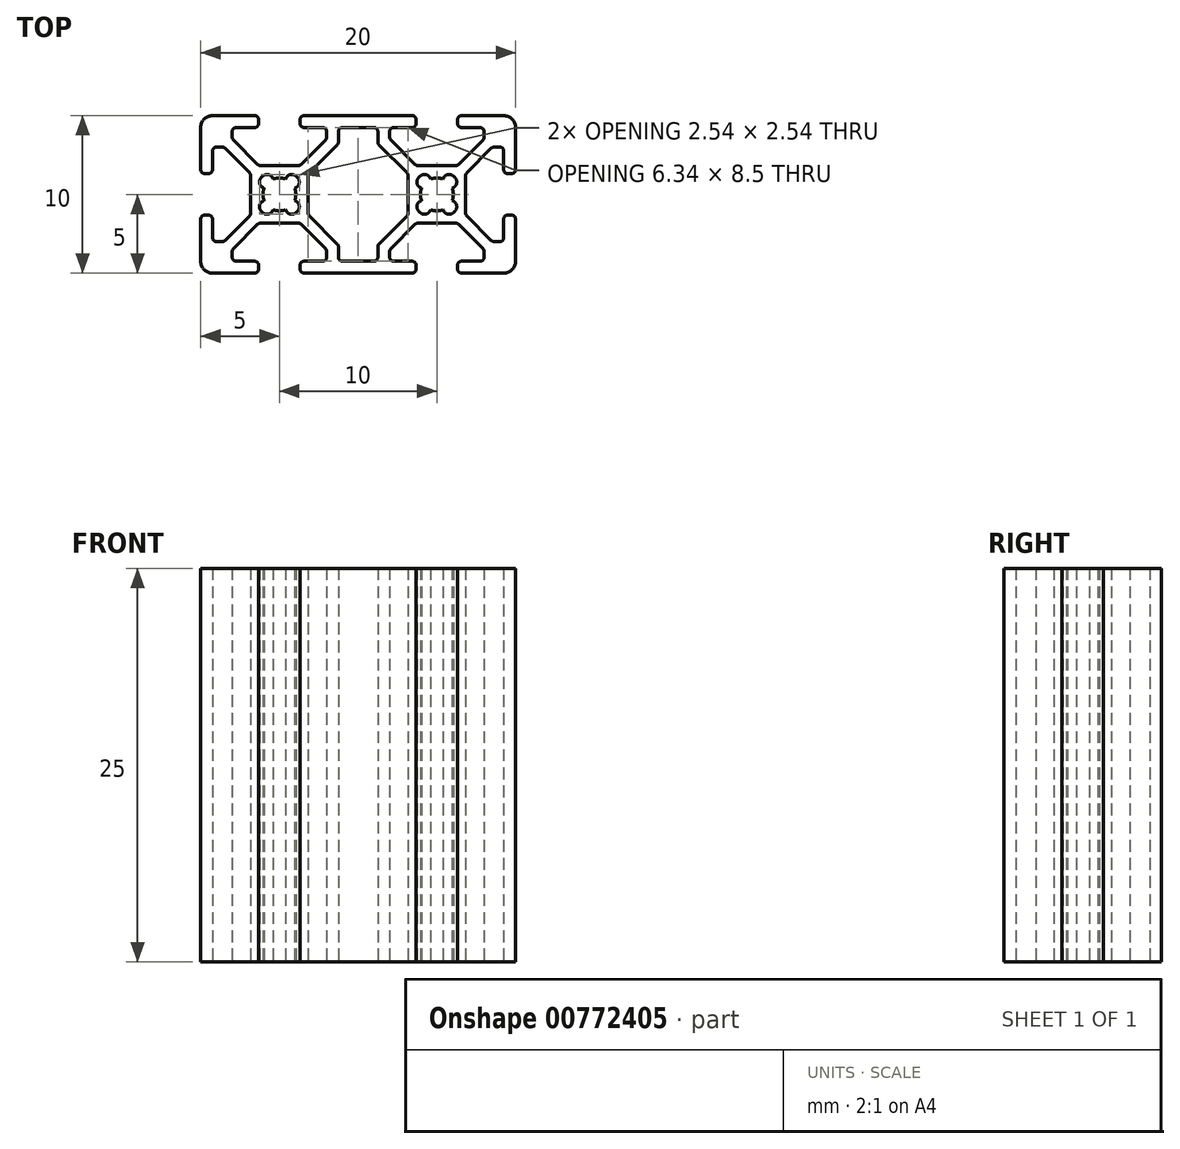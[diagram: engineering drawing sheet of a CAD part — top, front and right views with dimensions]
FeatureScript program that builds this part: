
annotation { "Feature Type Name" : "Feature", "Feature Type Description" : "" }
export const myFeature = defineFeature(function(context is Context, id is Id, definition is map)
    precondition{}
    {
        {
            var Q0;
            Q0=qCreatedBy(makeId("Top.planeOp"),FACE);
            var sketch = newSketch(context, id + "F0", { "sketchPlane" : qUnion([Q0])});
            skArc(sketch, "E0", {"start": v(-6.06, -1.15) * mm, "mid": v(-5.68, -1.25) * mm, "end": v(-5.4, -0.97) * mm});
            skLineSegment(sketch, "E1", {"start": v(-6.15, -1.06) * mm, "end": v(-6.06, -1.15) * mm});
            skArc(sketch, "E2", {"start": v(-5.97, -0.4) * mm, "mid": v(-6.25, -0.68) * mm, "end": v(-6.15, -1.06) * mm});
            skArc(sketch, "E3", {"start": v(-5.97, 0.4) * mm, "mid": v(-6.05, 0) * mm, "end": v(-5.97, -0.4) * mm});
            skArc(sketch, "E4", {"start": v(-6.15, 1.06) * mm, "mid": v(-6.25, 0.68) * mm, "end": v(-5.97, 0.4) * mm});
            skLineSegment(sketch, "E5", {"start": v(-6.06, 1.15) * mm, "end": v(-6.15, 1.06) * mm});
            skArc(sketch, "E6", {"start": v(-5.4, 0.97) * mm, "mid": v(-5.68, 1.25) * mm, "end": v(-6.06, 1.15) * mm});
            skArc(sketch, "E7", {"start": v(-4.6, 0.97) * mm, "mid": v(-5, 1.05) * mm, "end": v(-5.4, 0.97) * mm});
            skArc(sketch, "E8", {"start": v(-3.94, 1.15) * mm, "mid": v(-4.32, 1.25) * mm, "end": v(-4.6, 0.97) * mm});
            skLineSegment(sketch, "E9", {"start": v(-3.85, 1.06) * mm, "end": v(-3.94, 1.15) * mm});
            skArc(sketch, "E10", {"start": v(-4.03, 0.4) * mm, "mid": v(-3.75, 0.68) * mm, "end": v(-3.85, 1.06) * mm});
            skArc(sketch, "E11", {"start": v(-4.03, -0.4) * mm, "mid": v(-3.95, 0) * mm, "end": v(-4.03, 0.4) * mm});
            skArc(sketch, "E12", {"start": v(-3.85, -1.06) * mm, "mid": v(-3.75, -0.68) * mm, "end": v(-4.03, -0.4) * mm});
            skLineSegment(sketch, "E13", {"start": v(-3.94, -1.15) * mm, "end": v(-3.85, -1.06) * mm});
            skArc(sketch, "E14", {"start": v(-4.6, -0.97) * mm, "mid": v(-4.32, -1.25) * mm, "end": v(-3.94, -1.15) * mm});
            skArc(sketch, "E15", {"start": v(-5.4, -0.97) * mm, "mid": v(-5, -1.05) * mm, "end": v(-4.6, -0.97) * mm});
            skArc(sketch, "E16", {"start": v(-1.25, -4) * mm, "mid": v(-1.18, -4.18) * mm, "end": v(-1, -4.25) * mm});
            skLineSegment(sketch, "E17", {"start": v(-1.25, -3.32) * mm, "end": v(-1.25, -4) * mm});
            skArc(sketch, "E18", {"start": v(-1.25, -3.32) * mm, "mid": v(-1.27, -3.23) * mm, "end": v(-1.33, -3.14) * mm});
            skLineSegment(sketch, "E19", {"start": v(-3.1, -1.37) * mm, "end": v(-1.33, -3.14) * mm});
            skArc(sketch, "E20", {"start": v(-3.17, -1.2) * mm, "mid": v(-3.15, -1.29) * mm, "end": v(-3.1, -1.37) * mm});
            skLineSegment(sketch, "E21", {"start": v(-3.17, 1.2) * mm, "end": v(-3.17, -1.2) * mm});
            skArc(sketch, "E22", {"start": v(-3.1, 1.37) * mm, "mid": v(-3.15, 1.29) * mm, "end": v(-3.17, 1.2) * mm});
            skLineSegment(sketch, "E23", {"start": v(-1.33, 3.14) * mm, "end": v(-3.1, 1.37) * mm});
            skArc(sketch, "E24", {"start": v(-1.33, 3.14) * mm, "mid": v(-1.27, 3.23) * mm, "end": v(-1.25, 3.32) * mm});
            skLineSegment(sketch, "E25", {"start": v(-1.25, 4) * mm, "end": v(-1.25, 3.32) * mm});
            skArc(sketch, "E26", {"start": v(-1, 4.25) * mm, "mid": v(-1.18, 4.18) * mm, "end": v(-1.25, 4) * mm});
            skLineSegment(sketch, "E27", {"start": v(1, 4.25) * mm, "end": v(-1, 4.25) * mm});
            skArc(sketch, "E28", {"start": v(1.25, 4) * mm, "mid": v(1.18, 4.18) * mm, "end": v(1, 4.25) * mm});
            skLineSegment(sketch, "E29", {"start": v(1.25, 3.32) * mm, "end": v(1.25, 4) * mm});
            skArc(sketch, "E30", {"start": v(1.25, 3.32) * mm, "mid": v(1.27, 3.23) * mm, "end": v(1.33, 3.14) * mm});
            skLineSegment(sketch, "E31", {"start": v(3.1, 1.37) * mm, "end": v(1.33, 3.14) * mm});
            skArc(sketch, "E32", {"start": v(3.17, 1.2) * mm, "mid": v(3.15, 1.29) * mm, "end": v(3.1, 1.37) * mm});
            skLineSegment(sketch, "E33", {"start": v(3.17, -1.2) * mm, "end": v(3.17, 1.2) * mm});
            skArc(sketch, "E34", {"start": v(3.1, -1.37) * mm, "mid": v(3.15, -1.29) * mm, "end": v(3.17, -1.2) * mm});
            skLineSegment(sketch, "E35", {"start": v(1.33, -3.14) * mm, "end": v(3.1, -1.37) * mm});
            skArc(sketch, "E36", {"start": v(1.33, -3.14) * mm, "mid": v(1.27, -3.23) * mm, "end": v(1.25, -3.32) * mm});
            skLineSegment(sketch, "E37", {"start": v(1.25, -4) * mm, "end": v(1.25, -3.32) * mm});
            skArc(sketch, "E38", {"start": v(1, -4.25) * mm, "mid": v(1.18, -4.18) * mm, "end": v(1.25, -4) * mm});
            skLineSegment(sketch, "E39", {"start": v(-1, -4.25) * mm, "end": v(1, -4.25) * mm});
            skArc(sketch, "E40", {"start": v(3.94, -1.15) * mm, "mid": v(4.32, -1.25) * mm, "end": v(4.6, -0.97) * mm});
            skLineSegment(sketch, "E41", {"start": v(3.85, -1.06) * mm, "end": v(3.94, -1.15) * mm});
            skArc(sketch, "E42", {"start": v(4.03, -0.4) * mm, "mid": v(3.75, -0.68) * mm, "end": v(3.85, -1.06) * mm});
            skArc(sketch, "E43", {"start": v(4.03, 0.4) * mm, "mid": v(3.95, 0) * mm, "end": v(4.03, -0.4) * mm});
            skArc(sketch, "E44", {"start": v(3.85, 1.06) * mm, "mid": v(3.75, 0.68) * mm, "end": v(4.03, 0.4) * mm});
            skLineSegment(sketch, "E45", {"start": v(3.94, 1.15) * mm, "end": v(3.85, 1.06) * mm});
            skArc(sketch, "E46", {"start": v(4.6, 0.97) * mm, "mid": v(4.32, 1.25) * mm, "end": v(3.94, 1.15) * mm});
            skArc(sketch, "E47", {"start": v(5.4, 0.97) * mm, "mid": v(5, 1.05) * mm, "end": v(4.6, 0.97) * mm});
            skArc(sketch, "E48", {"start": v(6.06, 1.15) * mm, "mid": v(5.68, 1.25) * mm, "end": v(5.4, 0.97) * mm});
            skLineSegment(sketch, "E49", {"start": v(6.15, 1.06) * mm, "end": v(6.06, 1.15) * mm});
            skArc(sketch, "E50", {"start": v(5.97, 0.4) * mm, "mid": v(6.25, 0.68) * mm, "end": v(6.15, 1.06) * mm});
            skArc(sketch, "E51", {"start": v(5.97, -0.4) * mm, "mid": v(6.05, 0) * mm, "end": v(5.97, 0.4) * mm});
            skArc(sketch, "E52", {"start": v(6.15, -1.06) * mm, "mid": v(6.25, -0.68) * mm, "end": v(5.97, -0.4) * mm});
            skLineSegment(sketch, "E53", {"start": v(6.06, -1.15) * mm, "end": v(6.15, -1.06) * mm});
            skArc(sketch, "E54", {"start": v(5.4, -0.97) * mm, "mid": v(5.68, -1.25) * mm, "end": v(6.06, -1.15) * mm});
            skArc(sketch, "E55", {"start": v(4.6, -0.97) * mm, "mid": v(5, -1.05) * mm, "end": v(5.4, -0.97) * mm});
            skArc(sketch, "E56", {"start": v(-6.2, -1.83) * mm, "mid": v(-6.29, -1.85) * mm, "end": v(-6.37, -1.9) * mm});
            skLineSegment(sketch, "E57", {"start": v(-6.2, -1.83) * mm, "end": v(-3.8, -1.83) * mm});
            skArc(sketch, "E58", {"start": v(-3.63, -1.9) * mm, "mid": v(-3.71, -1.85) * mm, "end": v(-3.8, -1.83) * mm});
            skLineSegment(sketch, "E59", {"start": v(-3.63, -1.9) * mm, "end": v(-2.08, -3.45) * mm});
            skArc(sketch, "E60", {"start": v(-2, -3.63) * mm, "mid": v(-2.02, -3.54) * mm, "end": v(-2.08, -3.45) * mm});
            skLineSegment(sketch, "E61", {"start": v(-2, -3.63) * mm, "end": v(-2, -4) * mm});
            skArc(sketch, "E62", {"start": v(-2.26, -4.25) * mm, "mid": v(-2.08, -4.18) * mm, "end": v(-2, -4) * mm});
            skLineSegment(sketch, "E63", {"start": v(-2.26, -4.25) * mm, "end": v(-3.43, -4.25) * mm});
            skArc(sketch, "E64", {"start": v(-3.43, -4.25) * mm, "mid": v(-3.61, -4.32) * mm, "end": v(-3.69, -4.5) * mm});
            skLineSegment(sketch, "E65", {"start": v(-3.69, -4.5) * mm, "end": v(-3.69, -4.75) * mm});
            skArc(sketch, "E66", {"start": v(-3.69, -4.75) * mm, "mid": v(-3.61, -4.93) * mm, "end": v(-3.43, -5) * mm});
            skLineSegment(sketch, "E67", {"start": v(-3.43, -5) * mm, "end": v(3.43, -5) * mm});
            skArc(sketch, "E68", {"start": v(3.43, -5) * mm, "mid": v(3.61, -4.93) * mm, "end": v(3.69, -4.75) * mm});
            skLineSegment(sketch, "E69", {"start": v(3.69, -4.75) * mm, "end": v(3.69, -4.5) * mm});
            skArc(sketch, "E70", {"start": v(3.69, -4.5) * mm, "mid": v(3.61, -4.32) * mm, "end": v(3.43, -4.25) * mm});
            skLineSegment(sketch, "E71", {"start": v(3.43, -4.25) * mm, "end": v(2.26, -4.25) * mm});
            skArc(sketch, "E72", {"start": v(2, -4) * mm, "mid": v(2.08, -4.18) * mm, "end": v(2.26, -4.25) * mm});
            skLineSegment(sketch, "E73", {"start": v(2, -4) * mm, "end": v(2, -3.63) * mm});
            skArc(sketch, "E74", {"start": v(2.08, -3.45) * mm, "mid": v(2.02, -3.54) * mm, "end": v(2, -3.63) * mm});
            skLineSegment(sketch, "E75", {"start": v(2.08, -3.45) * mm, "end": v(3.63, -1.9) * mm});
            skArc(sketch, "E76", {"start": v(3.8, -1.83) * mm, "mid": v(3.71, -1.85) * mm, "end": v(3.63, -1.9) * mm});
            skLineSegment(sketch, "E77", {"start": v(3.8, -1.83) * mm, "end": v(6.2, -1.83) * mm});
            skArc(sketch, "E78", {"start": v(6.37, -1.9) * mm, "mid": v(6.29, -1.85) * mm, "end": v(6.2, -1.83) * mm});
            skLineSegment(sketch, "E79", {"start": v(6.37, -1.9) * mm, "end": v(7.92, -3.45) * mm});
            skArc(sketch, "E80", {"start": v(8, -3.63) * mm, "mid": v(7.98, -3.54) * mm, "end": v(7.92, -3.45) * mm});
            skLineSegment(sketch, "E81", {"start": v(8, -3.63) * mm, "end": v(8, -4) * mm});
            skArc(sketch, "E82", {"start": v(7.74, -4.25) * mm, "mid": v(7.92, -4.18) * mm, "end": v(8, -4) * mm});
            skLineSegment(sketch, "E83", {"start": v(7.74, -4.25) * mm, "end": v(6.57, -4.25) * mm});
            skArc(sketch, "E84", {"start": v(6.57, -4.25) * mm, "mid": v(6.39, -4.32) * mm, "end": v(6.32, -4.5) * mm});
            skLineSegment(sketch, "E85", {"start": v(6.32, -4.5) * mm, "end": v(6.32, -4.75) * mm});
            skArc(sketch, "E86", {"start": v(6.32, -4.75) * mm, "mid": v(6.39, -4.93) * mm, "end": v(6.57, -5) * mm});
            skLineSegment(sketch, "E87", {"start": v(6.57, -5) * mm, "end": v(9.25, -5) * mm});
            skArc(sketch, "E88", {"start": v(9.25, -5) * mm, "mid": v(9.78, -4.78) * mm, "end": v(10, -4.25) * mm});
            skLineSegment(sketch, "E89", {"start": v(10, -4.25) * mm, "end": v(10, -1.57) * mm});
            skArc(sketch, "E90", {"start": v(10, -1.57) * mm, "mid": v(9.93, -1.39) * mm, "end": v(9.75, -1.31) * mm});
            skLineSegment(sketch, "E91", {"start": v(9.75, -1.31) * mm, "end": v(9.5, -1.31) * mm});
            skArc(sketch, "E92", {"start": v(9.5, -1.31) * mm, "mid": v(9.32, -1.39) * mm, "end": v(9.25, -1.57) * mm});
            skLineSegment(sketch, "E93", {"start": v(9.25, -1.57) * mm, "end": v(9.25, -2.74) * mm});
            skArc(sketch, "E94", {"start": v(9, -3) * mm, "mid": v(9.18, -2.92) * mm, "end": v(9.25, -2.74) * mm});
            skLineSegment(sketch, "E95", {"start": v(9, -3) * mm, "end": v(8.63, -3) * mm});
            skArc(sketch, "E96", {"start": v(8.45, -2.92) * mm, "mid": v(8.54, -2.98) * mm, "end": v(8.63, -3) * mm});
            skLineSegment(sketch, "E97", {"start": v(8.45, -2.92) * mm, "end": v(6.9, -1.37) * mm});
            skArc(sketch, "E98", {"start": v(6.83, -1.2) * mm, "mid": v(6.85, -1.29) * mm, "end": v(6.9, -1.37) * mm});
            skLineSegment(sketch, "E99", {"start": v(6.83, -1.2) * mm, "end": v(6.83, 1.2) * mm});
            skArc(sketch, "E100", {"start": v(6.9, 1.37) * mm, "mid": v(6.85, 1.29) * mm, "end": v(6.83, 1.2) * mm});
            skLineSegment(sketch, "E101", {"start": v(6.9, 1.37) * mm, "end": v(8.45, 2.92) * mm});
            skArc(sketch, "E102", {"start": v(8.63, 3) * mm, "mid": v(8.54, 2.98) * mm, "end": v(8.45, 2.92) * mm});
            skLineSegment(sketch, "E103", {"start": v(8.63, 3) * mm, "end": v(9, 3) * mm});
            skArc(sketch, "E104", {"start": v(9.25, 2.74) * mm, "mid": v(9.18, 2.92) * mm, "end": v(9, 3) * mm});
            skLineSegment(sketch, "E105", {"start": v(9.25, 2.74) * mm, "end": v(9.25, 1.57) * mm});
            skArc(sketch, "E106", {"start": v(9.25, 1.57) * mm, "mid": v(9.32, 1.39) * mm, "end": v(9.5, 1.31) * mm});
            skLineSegment(sketch, "E107", {"start": v(9.5, 1.31) * mm, "end": v(9.75, 1.31) * mm});
            skArc(sketch, "E108", {"start": v(9.75, 1.31) * mm, "mid": v(9.93, 1.39) * mm, "end": v(10, 1.57) * mm});
            skLineSegment(sketch, "E109", {"start": v(10, 1.57) * mm, "end": v(10, 4.25) * mm});
            skArc(sketch, "E110", {"start": v(10, 4.25) * mm, "mid": v(9.78, 4.78) * mm, "end": v(9.25, 5) * mm});
            skLineSegment(sketch, "E111", {"start": v(9.25, 5) * mm, "end": v(6.57, 5) * mm});
            skArc(sketch, "E112", {"start": v(6.57, 5) * mm, "mid": v(6.39, 4.93) * mm, "end": v(6.32, 4.75) * mm});
            skLineSegment(sketch, "E113", {"start": v(6.32, 4.75) * mm, "end": v(6.32, 4.5) * mm});
            skArc(sketch, "E114", {"start": v(6.32, 4.5) * mm, "mid": v(6.39, 4.32) * mm, "end": v(6.57, 4.25) * mm});
            skLineSegment(sketch, "E115", {"start": v(6.57, 4.25) * mm, "end": v(7.74, 4.25) * mm});
            skArc(sketch, "E116", {"start": v(8, 4) * mm, "mid": v(7.92, 4.18) * mm, "end": v(7.74, 4.25) * mm});
            skLineSegment(sketch, "E117", {"start": v(8, 4) * mm, "end": v(8, 3.63) * mm});
            skArc(sketch, "E118", {"start": v(7.92, 3.45) * mm, "mid": v(7.98, 3.54) * mm, "end": v(8, 3.63) * mm});
            skLineSegment(sketch, "E119", {"start": v(7.92, 3.45) * mm, "end": v(6.37, 1.9) * mm});
            skArc(sketch, "E120", {"start": v(6.2, 1.83) * mm, "mid": v(6.29, 1.85) * mm, "end": v(6.37, 1.9) * mm});
            skLineSegment(sketch, "E121", {"start": v(6.2, 1.83) * mm, "end": v(3.8, 1.83) * mm});
            skArc(sketch, "E122", {"start": v(3.63, 1.9) * mm, "mid": v(3.71, 1.85) * mm, "end": v(3.8, 1.83) * mm});
            skLineSegment(sketch, "E123", {"start": v(3.63, 1.9) * mm, "end": v(2.08, 3.45) * mm});
            skArc(sketch, "E124", {"start": v(2, 3.63) * mm, "mid": v(2.02, 3.54) * mm, "end": v(2.08, 3.45) * mm});
            skLineSegment(sketch, "E125", {"start": v(2, 3.63) * mm, "end": v(2, 4) * mm});
            skArc(sketch, "E126", {"start": v(2.26, 4.25) * mm, "mid": v(2.08, 4.18) * mm, "end": v(2, 4) * mm});
            skLineSegment(sketch, "E127", {"start": v(2.26, 4.25) * mm, "end": v(3.43, 4.25) * mm});
            skArc(sketch, "E128", {"start": v(3.43, 4.25) * mm, "mid": v(3.61, 4.32) * mm, "end": v(3.69, 4.5) * mm});
            skLineSegment(sketch, "E129", {"start": v(3.69, 4.5) * mm, "end": v(3.69, 4.75) * mm});
            skArc(sketch, "E130", {"start": v(3.69, 4.75) * mm, "mid": v(3.61, 4.93) * mm, "end": v(3.43, 5) * mm});
            skLineSegment(sketch, "E131", {"start": v(3.43, 5) * mm, "end": v(-3.43, 5) * mm});
            skArc(sketch, "E132", {"start": v(-3.43, 5) * mm, "mid": v(-3.61, 4.93) * mm, "end": v(-3.69, 4.75) * mm});
            skLineSegment(sketch, "E133", {"start": v(-3.69, 4.75) * mm, "end": v(-3.69, 4.5) * mm});
            skArc(sketch, "E134", {"start": v(-3.69, 4.5) * mm, "mid": v(-3.61, 4.32) * mm, "end": v(-3.43, 4.25) * mm});
            skLineSegment(sketch, "E135", {"start": v(-3.43, 4.25) * mm, "end": v(-2.26, 4.25) * mm});
            skArc(sketch, "E136", {"start": v(-2, 4) * mm, "mid": v(-2.08, 4.18) * mm, "end": v(-2.26, 4.25) * mm});
            skLineSegment(sketch, "E137", {"start": v(-2, 4) * mm, "end": v(-2, 3.63) * mm});
            skArc(sketch, "E138", {"start": v(-2.08, 3.45) * mm, "mid": v(-2.02, 3.54) * mm, "end": v(-2, 3.63) * mm});
            skLineSegment(sketch, "E139", {"start": v(-2.08, 3.45) * mm, "end": v(-3.63, 1.9) * mm});
            skArc(sketch, "E140", {"start": v(-3.8, 1.83) * mm, "mid": v(-3.71, 1.85) * mm, "end": v(-3.63, 1.9) * mm});
            skLineSegment(sketch, "E141", {"start": v(-3.8, 1.83) * mm, "end": v(-6.2, 1.83) * mm});
            skArc(sketch, "E142", {"start": v(-6.37, 1.9) * mm, "mid": v(-6.29, 1.85) * mm, "end": v(-6.2, 1.83) * mm});
            skLineSegment(sketch, "E143", {"start": v(-6.37, 1.9) * mm, "end": v(-7.92, 3.45) * mm});
            skArc(sketch, "E144", {"start": v(-8, 3.63) * mm, "mid": v(-7.98, 3.54) * mm, "end": v(-7.92, 3.45) * mm});
            skLineSegment(sketch, "E145", {"start": v(-8, 3.63) * mm, "end": v(-8, 4) * mm});
            skArc(sketch, "E146", {"start": v(-7.74, 4.25) * mm, "mid": v(-7.92, 4.18) * mm, "end": v(-8, 4) * mm});
            skLineSegment(sketch, "E147", {"start": v(-7.74, 4.25) * mm, "end": v(-6.57, 4.25) * mm});
            skArc(sketch, "E148", {"start": v(-6.57, 4.25) * mm, "mid": v(-6.39, 4.32) * mm, "end": v(-6.32, 4.5) * mm});
            skLineSegment(sketch, "E149", {"start": v(-6.32, 4.5) * mm, "end": v(-6.32, 4.75) * mm});
            skArc(sketch, "E150", {"start": v(-6.32, 4.75) * mm, "mid": v(-6.39, 4.93) * mm, "end": v(-6.57, 5) * mm});
            skLineSegment(sketch, "E151", {"start": v(-6.57, 5) * mm, "end": v(-9.25, 5) * mm});
            skArc(sketch, "E152", {"start": v(-9.25, 5) * mm, "mid": v(-9.78, 4.78) * mm, "end": v(-10, 4.25) * mm});
            skLineSegment(sketch, "E153", {"start": v(-10, 4.25) * mm, "end": v(-10, 1.57) * mm});
            skArc(sketch, "E154", {"start": v(-10, 1.57) * mm, "mid": v(-9.93, 1.39) * mm, "end": v(-9.75, 1.31) * mm});
            skLineSegment(sketch, "E155", {"start": v(-9.75, 1.31) * mm, "end": v(-9.5, 1.31) * mm});
            skArc(sketch, "E156", {"start": v(-9.5, 1.31) * mm, "mid": v(-9.32, 1.39) * mm, "end": v(-9.25, 1.57) * mm});
            skLineSegment(sketch, "E157", {"start": v(-9.25, 1.57) * mm, "end": v(-9.25, 2.74) * mm});
            skArc(sketch, "E158", {"start": v(-9, 3) * mm, "mid": v(-9.18, 2.92) * mm, "end": v(-9.25, 2.74) * mm});
            skLineSegment(sketch, "E159", {"start": v(-9, 3) * mm, "end": v(-8.63, 3) * mm});
            skArc(sketch, "E160", {"start": v(-8.45, 2.92) * mm, "mid": v(-8.54, 2.98) * mm, "end": v(-8.63, 3) * mm});
            skLineSegment(sketch, "E161", {"start": v(-8.45, 2.92) * mm, "end": v(-6.9, 1.37) * mm});
            skArc(sketch, "E162", {"start": v(-6.83, 1.2) * mm, "mid": v(-6.85, 1.29) * mm, "end": v(-6.9, 1.37) * mm});
            skLineSegment(sketch, "E163", {"start": v(-6.83, 1.2) * mm, "end": v(-6.83, -1.2) * mm});
            skArc(sketch, "E164", {"start": v(-6.9, -1.37) * mm, "mid": v(-6.85, -1.29) * mm, "end": v(-6.83, -1.2) * mm});
            skLineSegment(sketch, "E165", {"start": v(-6.9, -1.37) * mm, "end": v(-8.45, -2.92) * mm});
            skArc(sketch, "E166", {"start": v(-8.63, -3) * mm, "mid": v(-8.54, -2.98) * mm, "end": v(-8.45, -2.92) * mm});
            skLineSegment(sketch, "E167", {"start": v(-8.63, -3) * mm, "end": v(-9, -3) * mm});
            skArc(sketch, "E168", {"start": v(-9.25, -2.74) * mm, "mid": v(-9.18, -2.92) * mm, "end": v(-9, -3) * mm});
            skLineSegment(sketch, "E169", {"start": v(-9.25, -2.74) * mm, "end": v(-9.25, -1.57) * mm});
            skArc(sketch, "E170", {"start": v(-9.25, -1.57) * mm, "mid": v(-9.32, -1.39) * mm, "end": v(-9.5, -1.31) * mm});
            skLineSegment(sketch, "E171", {"start": v(-9.5, -1.31) * mm, "end": v(-9.75, -1.31) * mm});
            skArc(sketch, "E172", {"start": v(-9.75, -1.31) * mm, "mid": v(-9.93, -1.39) * mm, "end": v(-10, -1.57) * mm});
            skLineSegment(sketch, "E173", {"start": v(-10, -1.57) * mm, "end": v(-10, -4.25) * mm});
            skArc(sketch, "E174", {"start": v(-10, -4.25) * mm, "mid": v(-9.78, -4.78) * mm, "end": v(-9.25, -5) * mm});
            skLineSegment(sketch, "E175", {"start": v(-9.25, -5) * mm, "end": v(-6.57, -5) * mm});
            skArc(sketch, "E176", {"start": v(-6.57, -5) * mm, "mid": v(-6.39, -4.93) * mm, "end": v(-6.32, -4.75) * mm});
            skLineSegment(sketch, "E177", {"start": v(-6.32, -4.75) * mm, "end": v(-6.32, -4.5) * mm});
            skArc(sketch, "E178", {"start": v(-6.32, -4.5) * mm, "mid": v(-6.39, -4.32) * mm, "end": v(-6.57, -4.25) * mm});
            skLineSegment(sketch, "E179", {"start": v(-6.57, -4.25) * mm, "end": v(-7.74, -4.25) * mm});
            skArc(sketch, "E180", {"start": v(-8, -4) * mm, "mid": v(-7.92, -4.18) * mm, "end": v(-7.74, -4.25) * mm});
            skLineSegment(sketch, "E181", {"start": v(-8, -4) * mm, "end": v(-8, -3.63) * mm});
            skArc(sketch, "E182", {"start": v(-7.92, -3.45) * mm, "mid": v(-7.98, -3.54) * mm, "end": v(-8, -3.63) * mm});
            skLineSegment(sketch, "E183", {"start": v(-7.92, -3.45) * mm, "end": v(-6.37, -1.9) * mm});
            skSolve(sketch);
        }
        {
            var Q0;
            Q0=makeQuery(id+"F0.imprint","IMPRINT",FACE,{"disambiguationData":[TD([[makeQuery(id+"F0.imprint","IMPRINT",EDGE,{"derivedFrom":sQuery(id+"F0.wireOp",EDGE,"E0")}),-1.0]])]});
            extrude(context, id + "F1", {"entities" : qUnion([Q0]), "depth" : 25 * mm, "offsetDistance" : 25 * mm});
        }
    });
